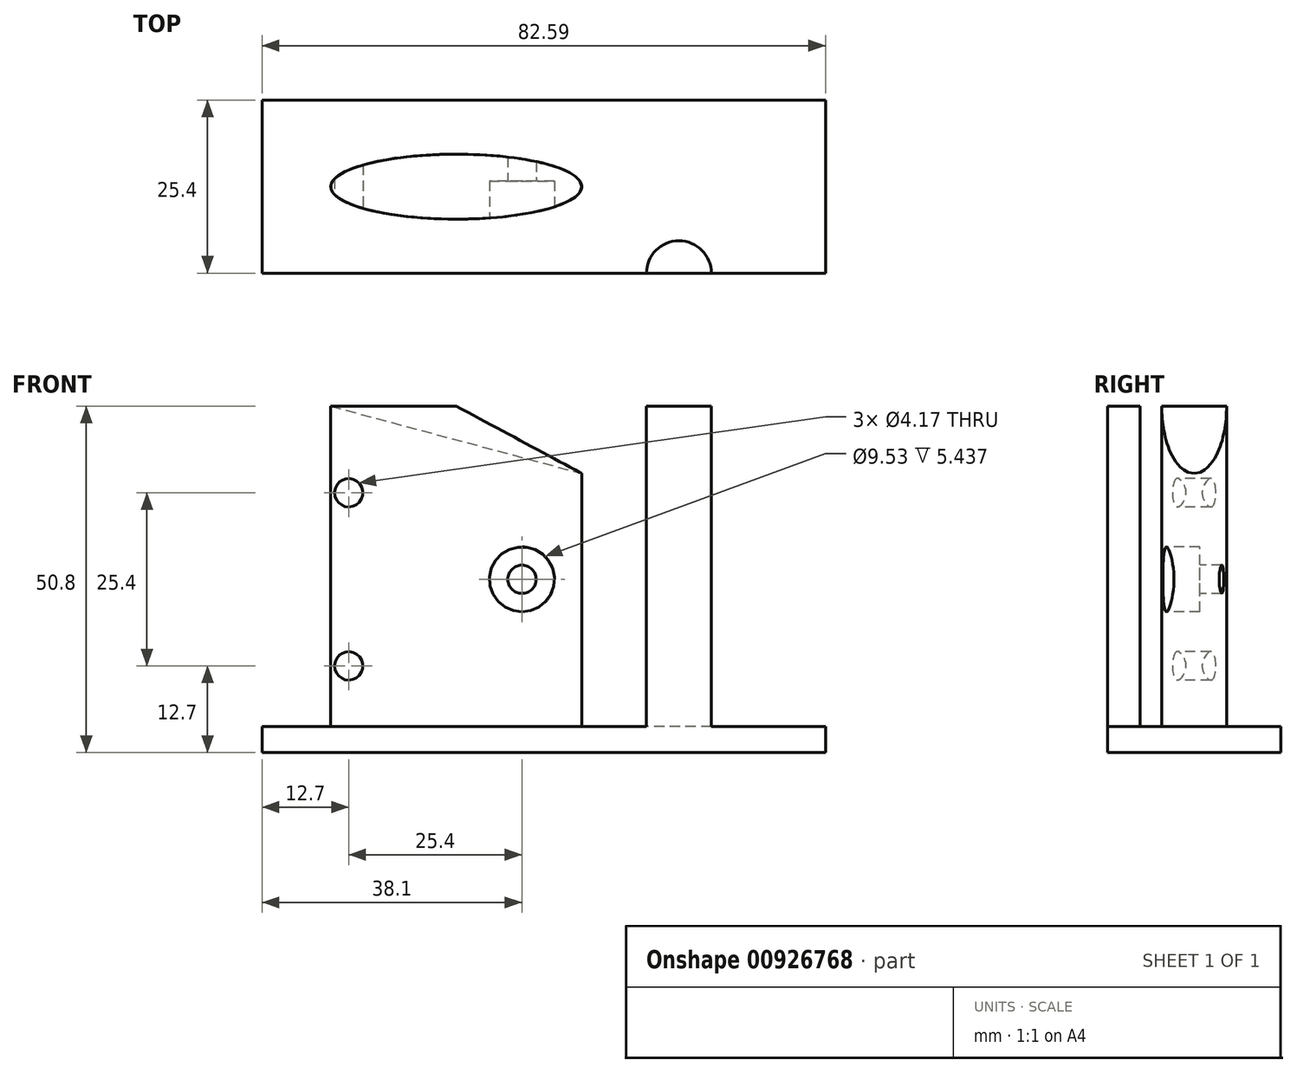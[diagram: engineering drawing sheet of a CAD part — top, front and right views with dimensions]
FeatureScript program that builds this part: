
annotation { "Feature Type Name" : "Feature", "Feature Type Description" : "" }
export const myFeature = defineFeature(function(context is Context, id is Id, definition is map)
    precondition{}
    {
        {
            var Q0;
            Q0=qCreatedBy(makeId("Front.planeOp"),FACE);
            var sketch = newSketch(context, id + "F0", { "sketchPlane" : qUnion([Q0])});
            skLineSegment(sketch, "E0.bottom", {"start": v(38.1, -25.4) * mm, "end": v(-38.1, -25.4) * mm});
            skLineSegment(sketch, "E0.top", {"start": v(38.1, 25.4) * mm, "end": v(-38.1, 25.4) * mm});
            skLineSegment(sketch, "E0.left", {"start": v(38.1, -25.4) * mm, "end": v(38.1, 25.4) * mm});
            skLineSegment(sketch, "E0.right", {"start": v(-38.1, -25.4) * mm, "end": v(-38.1, 25.4) * mm});
            skPoint(sketch, "E0.middle", {"position": v(0, 0) * mm});
            skSolve(sketch);
        }
        {
            var Q0;
            Q0 = qSketchRegion(id + "F0", true);
            extrude(context, id + "F1", {"entities" : qUnion([Q0]), "depth" : 25.4 * mm, "offsetDistance" : 25.4 * mm});
        }
        {
            var Q0;
            Q0=makeQuery(id+"F1.opExtrude","CAP_FACE",FACE,{"disambiguationData":[OSD([sQuery(id+"F0.wireOp",EDGE,"E0.bottom"),sQuery(id+"F0.wireOp",EDGE,"E0.top"),sQuery(id+"F0.wireOp",EDGE,"E0.left"),sQuery(id+"F0.wireOp",EDGE,"E0.right")])],"isStart":false});
            var sketch = newSketch(context, id + "F2", { "sketchPlane" : qUnion([Q0])});
            skLineSegment(sketch, "E1", {"start": v(38.1, 25.4) * mm, "end": v(24.49, -25.4) * mm});
            skLineSegment(sketch, "E2", {"start": v(24.49, -25.4) * mm, "end": v(38.1, -25.4) * mm});
            skLineSegment(sketch, "E3", {"start": v(38.1, -25.4) * mm, "end": v(38.1, 25.4) * mm});
            skSolve(sketch);
        }
        {
            var Q0;
            Q0 = qSketchRegion(id + "F2", true);
            extrude(context, id + "F3", {"entities" : qUnion([Q0]), "operationType" : NewBodyOperationType.REMOVE, "endBound" : BoundingType.THROUGH_ALL, "oppositeDirection" : true, "depth" : 25.4 * mm, "offsetDistance" : 25.4 * mm});
        }
        {
            var Q0;
            Q0=makeQuery(id+"F3.boolean.opBoolean","COPY",FACE,{"derivedFrom":makeQuery(id+"F3.opExtrude","SWEPT_FACE",FACE,{"disambiguationData":[OSD([sQuery(id+"F2.wireOp",EDGE,"E1")])]})});
            var sketch = newSketch(context, id + "F4", { "sketchPlane" : qUnion([Q0])});
            skPoint(sketch, "E4", {"position": v(-12.7, 22.04) * mm});
            skSolve(sketch);
        }
        {
            var Q0;
            Q0=sQuery(id+"F4.wireOp",VERTEX,"E4");
            var Q1;
            Q1=makeQuery(id+"F1.opExtrude","SWEPT_BODY",BODY,{"disambiguationData":[OSD([sQuery(id+"F0.wireOp",EDGE,"E0.bottom"),sQuery(id+"F0.wireOp",EDGE,"E0.top"),sQuery(id+"F0.wireOp",EDGE,"E0.left"),sQuery(id+"F0.wireOp",EDGE,"E0.right")])]});
            hole(context, id + "F5", {"style" : HoleStyle.SIMPLE, "endStyle" : HoleEndStyle.THROUGH, "holeDiameter" : 9.52 * mm, "majorDiameter" : 6.35 * mm, "isTappedThrough" : true, "tappedDepth" : 12.7 * mm, "tapClearance" : 3, "locations" : qUnion([Q0]), "scope" : qUnion([Q1])});
        }
        {
            var Q0;
            Q0=makeQuery(id+"F1.opExtrude","CAP_FACE",FACE,{"disambiguationData":[OSD([sQuery(id+"F0.wireOp",EDGE,"E0.bottom"),sQuery(id+"F0.wireOp",EDGE,"E0.top"),sQuery(id+"F0.wireOp",EDGE,"E0.left"),sQuery(id+"F0.wireOp",EDGE,"E0.right")])],"isStart":true});
            var sketch = newSketch(context, id + "F6", { "sketchPlane" : qUnion([Q0])});
            skLineSegment(sketch, "E5", {"start": v(-38.1, 25.4) * mm, "end": v(-24.49, -25.4) * mm});
            skLineSegment(sketch, "E6", {"start": v(-24.49, -25.4) * mm, "end": v(-38.1, -25.4) * mm});
            skLineSegment(sketch, "E7", {"start": v(-38.1, -25.4) * mm, "end": v(-38.1, 25.4) * mm});
            skLineSegment(sketch, "E8", {"start": v(-24.49, -25.4) * mm, "end": v(-24.49, 25.4) * mm});
            skLineSegment(sketch, "E9", {"start": v(-24.49, 25.4) * mm, "end": v(-38.1, 25.4) * mm});
            skSolve(sketch);
        }
        {
            var Q0;
            Q0=makeQuery(id+"F6.imprint","IMPRINT",FACE,{"disambiguationData":[TD([[makeQuery(id+"F6.imprint","IMPRINT",EDGE,{"derivedFrom":sQuery(id+"F6.wireOp",EDGE,"E5")}),1.0]])]});
            extrude(context, id + "F7", {"entities" : qUnion([Q0]), "operationType" : NewBodyOperationType.REMOVE, "endBound" : BoundingType.THROUGH_ALL, "oppositeDirection" : true, "depth" : 25.4 * mm, "offsetDistance" : 25.4 * mm});
        }
        {
            var Q0;
            Q0=makeQuery(id+"F1.opExtrude","CAP_FACE",FACE,{"disambiguationData":[OSD([sQuery(id+"F0.wireOp",EDGE,"E0.bottom"),sQuery(id+"F0.wireOp",EDGE,"E0.top"),sQuery(id+"F0.wireOp",EDGE,"E0.left"),sQuery(id+"F0.wireOp",EDGE,"E0.right")])],"isStart":false});
            var sketch = newSketch(context, id + "F8", { "sketchPlane" : qUnion([Q0])});
            skLineSegment(sketch, "E10", {"start": v(24.49, 25.4) * mm, "end": v(10.88, -25.4) * mm});
            skLineSegment(sketch, "E11", {"start": v(10.88, -25.4) * mm, "end": v(24.49, -25.4) * mm});
            skLineSegment(sketch, "E12", {"start": v(24.49, -25.4) * mm, "end": v(24.49, 25.4) * mm});
            skSolve(sketch);
        }
        {
            var Q0;
            Q0 = qSketchRegion(id + "F8", true);
            extrude(context, id + "F9", {"entities" : qUnion([Q0]), "operationType" : NewBodyOperationType.REMOVE, "endBound" : BoundingType.THROUGH_ALL, "oppositeDirection" : true, "depth" : 25.4 * mm, "offsetDistance" : 25.4 * mm});
        }
        {
            var Q0;
            Q0=makeQuery(id+"F1.opExtrude","CAP_FACE",FACE,{"disambiguationData":[OSD([sQuery(id+"F0.wireOp",EDGE,"E0.bottom"),sQuery(id+"F0.wireOp",EDGE,"E0.top"),sQuery(id+"F0.wireOp",EDGE,"E0.left"),sQuery(id+"F0.wireOp",EDGE,"E0.right")])],"isStart":false});
            var sketch = newSketch(context, id + "F10", { "sketchPlane" : qUnion([Q0])});
            skLineSegment(sketch, "E13", {"start": v(24.49, 25.4) * mm, "end": v(44.5, 25.4) * mm});
            skLineSegment(sketch, "E14", {"start": v(44.5, 25.4) * mm, "end": v(44.5, -25.4) * mm});
            skLineSegment(sketch, "E15", {"start": v(44.5, -25.4) * mm, "end": v(10.88, -25.4) * mm});
            skLineSegment(sketch, "E16", {"start": v(10.88, -25.4) * mm, "end": v(24.49, 25.4) * mm});
            skSolve(sketch);
        }
        {
            var Q0;
            Q0=makeQuery(id+"F10.imprint","IMPRINT",FACE,{"disambiguationData":[TD([[makeQuery(id+"F10.imprint","IMPRINT",EDGE,{"derivedFrom":sQuery(id+"F10.wireOp",EDGE,"E13")}),-1.0]])]});
            extrude(context, id + "F11", {"entities" : qUnion([Q0]), "operationType" : NewBodyOperationType.ADD, "oppositeDirection" : true, "depth" : 25.4 * mm, "offsetDistance" : 25.4 * mm});
        }
        {
            var Q0;
            Q0=makeQuery(id+"F11.opExtrude","SWEPT_FACE",FACE,{"disambiguationData":[OSD([sQuery(id+"F10.wireOp",EDGE,"E16")])]});
            var sketch = newSketch(context, id + "F12", { "sketchPlane" : qUnion([Q0])});
            skPoint(sketch, "E17", {"position": v(12.7, 22.04) * mm});
            skSolve(sketch);
        }
        {
            var Q0;
            Q0=sQuery(id+"F12.wireOp",VERTEX,"E17");
            var Q1;
            Q1=makeQuery(id+"F1.opExtrude","SWEPT_BODY",BODY,{"disambiguationData":[OSD([sQuery(id+"F0.wireOp",EDGE,"E0.bottom"),sQuery(id+"F0.wireOp",EDGE,"E0.top"),sQuery(id+"F0.wireOp",EDGE,"E0.left"),sQuery(id+"F0.wireOp",EDGE,"E0.right")])]});
            hole(context, id + "F13", {"style" : HoleStyle.SIMPLE, "endStyle" : HoleEndStyle.THROUGH, "holeDiameter" : 3.17 * mm, "majorDiameter" : 6.35 * mm, "isTappedThrough" : true, "tappedDepth" : 12.7 * mm, "tapClearance" : 3, "locations" : qUnion([Q0]), "scope" : qUnion([Q1])});
        }
        {
            var Q0;
            Q0=makeQuery(id+"F11.boolean.opBoolean","MERGE",FACE,{"derivedFrom":[makeQuery(id+"F1.opExtrude","SWEPT_FACE",FACE,{"disambiguationData":[OSD([sQuery(id+"F0.wireOp",EDGE,"E0.top")])]}),makeQuery(id+"F11.opExtrude","SWEPT_FACE",FACE,{"disambiguationData":[OSD([sQuery(id+"F10.wireOp",EDGE,"E13")])]})]});
            var sketch = newSketch(context, id + "F14", { "sketchPlane" : qUnion([Q0])});
            skArc(sketch, "E18", {"start": v(18.25, -25.4) * mm, "mid": v(23.01, -20.64) * mm, "end": v(27.78, -25.4) * mm});
            skSolve(sketch);
        }
        {
            var Q0;
            Q0 = qSketchRegion(id + "F14", true);
            var Q1;
            {var subQ0=sQuery(id+"F14.wireOp",EDGE,"E18");Q1=makeQuery(id+"F14.imprint","IMPRINT",FACE,{"disambiguationData":[TD([[makeQuery(id+"F14.imprint","IMPRINT",EDGE,{"derivedFrom":subQ0}),-1.0]])]});}
            extrude(context, id + "F15", {"entities" : qUnion([Q0, Q1]), "operationType" : NewBodyOperationType.REMOVE, "oppositeDirection" : true, "depth" : 47 * mm, "offsetDistance" : 25.4 * mm});
        }
        {
            var Q0;
            Q0=makeQuery(id+"F11.boolean.opBoolean","MERGE",FACE,{"derivedFrom":[makeQuery(id+"F1.opExtrude","CAP_FACE",FACE,{"disambiguationData":[OSD([sQuery(id+"F0.wireOp",EDGE,"E0.bottom"),sQuery(id+"F0.wireOp",EDGE,"E0.top"),sQuery(id+"F0.wireOp",EDGE,"E0.left"),sQuery(id+"F0.wireOp",EDGE,"E0.right")])],"isStart":false}),makeQuery(id+"F11.opExtrude","CAP_FACE",FACE,{"disambiguationData":[OSD([sQuery(id+"F10.wireOp",EDGE,"E13"),sQuery(id+"F10.wireOp",EDGE,"E14"),sQuery(id+"F10.wireOp",EDGE,"E15"),sQuery(id+"F10.wireOp",EDGE,"E16")])],"isStart":true})]});
            var sketch = newSketch(context, id + "F16", { "sketchPlane" : qUnion([Q0])});
            skPoint(sketch, "E19", {"position": v(-25.4, -12.7) * mm});
            skPoint(sketch, "E20", {"position": v(-25.4, 12.7) * mm});
            skPoint(sketch, "E21", {"position": v(0, 0) * mm});
            skSolve(sketch);
        }
        {
            var Q0;
            Q0=sQuery(id+"F16.wireOp",VERTEX,"E19");
            var Q1;
            Q1=sQuery(id+"F16.wireOp",VERTEX,"E20");
            var Q2;
            Q2=sQuery(id+"F16.wireOp",VERTEX,"E21");
            var Q3;
            Q3=makeQuery(id+"F1.opExtrude","SWEPT_BODY",BODY,{"disambiguationData":[OSD([sQuery(id+"F0.wireOp",EDGE,"E0.bottom"),sQuery(id+"F0.wireOp",EDGE,"E0.top"),sQuery(id+"F0.wireOp",EDGE,"E0.left"),sQuery(id+"F0.wireOp",EDGE,"E0.right")])]});
            hole(context, id + "F17", {"style" : HoleStyle.C_BORE, "endStyle" : HoleEndStyle.THROUGH, "holeDiameter" : 4.17 * mm, "cBoreDiameter" : 9.52 * mm, "cBoreDepth" : 3.8 * mm, "majorDiameter" : 6.35 * mm, "isTappedThrough" : true, "tappedDepth" : 12.7 * mm, "tapClearance" : 3, "locations" : qUnion([Q0, Q1, Q2]), "scope" : qUnion([Q3])});
        }
    });
